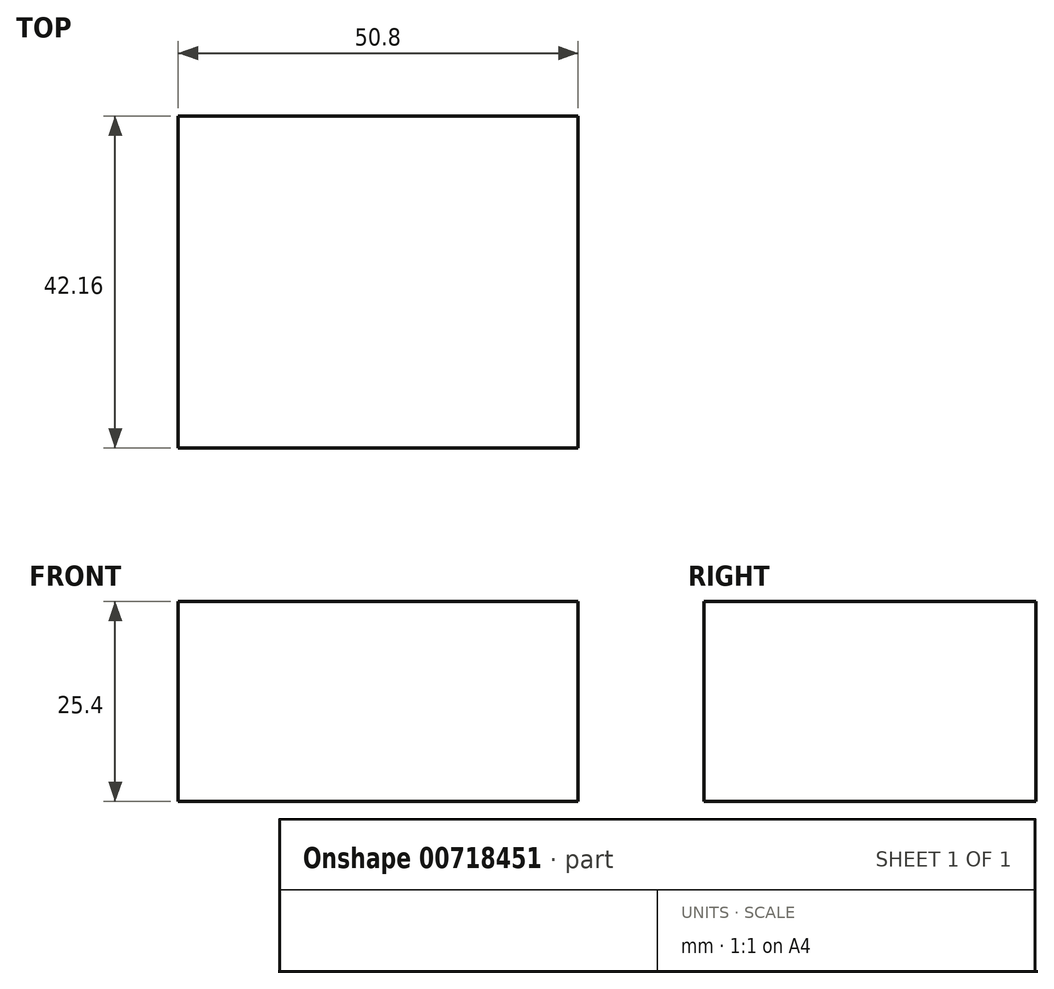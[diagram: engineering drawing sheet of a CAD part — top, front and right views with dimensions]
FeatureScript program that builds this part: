
annotation { "Feature Type Name" : "Feature", "Feature Type Description" : "" }
export const myFeature = defineFeature(function(context is Context, id is Id, definition is map)
    precondition{}
    {
        {
            var Q0;
            Q0=qCreatedBy(makeId("Front.planeOp"),FACE);
            var sketch = newSketch(context, id + "F0", { "sketchPlane" : qUnion([Q0])});
            skLineSegment(sketch, "E0", {"start": v(-37.12, 0) * mm, "end": v(-37.12, 25.4) * mm});
            skLineSegment(sketch, "E1", {"start": v(-37.12, 25.4) * mm, "end": v(-11.72, 25.4) * mm});
            skLineSegment(sketch, "E2", {"start": v(-11.72, 25.4) * mm, "end": v(-11.72, 0) * mm});
            skLineSegment(sketch, "E3", {"start": v(-11.72, 25.4) * mm, "end": v(13.68, 25.4) * mm});
            skLineSegment(sketch, "E4", {"start": v(13.68, 25.4) * mm, "end": v(13.68, 0) * mm});
            skLineSegment(sketch, "E5", {"start": v(13.68, 0) * mm, "end": v(-37.12, 0) * mm});
            skSolve(sketch);
        }
        {
            var Q0;
            Q0 = qSketchRegion(id + "F0", true);
            extrude(context, id + "F1", {"entities" : qUnion([Q0]), "depth" : 42.16 * mm, "offsetDistance" : 25.4 * mm});
        }
    });
